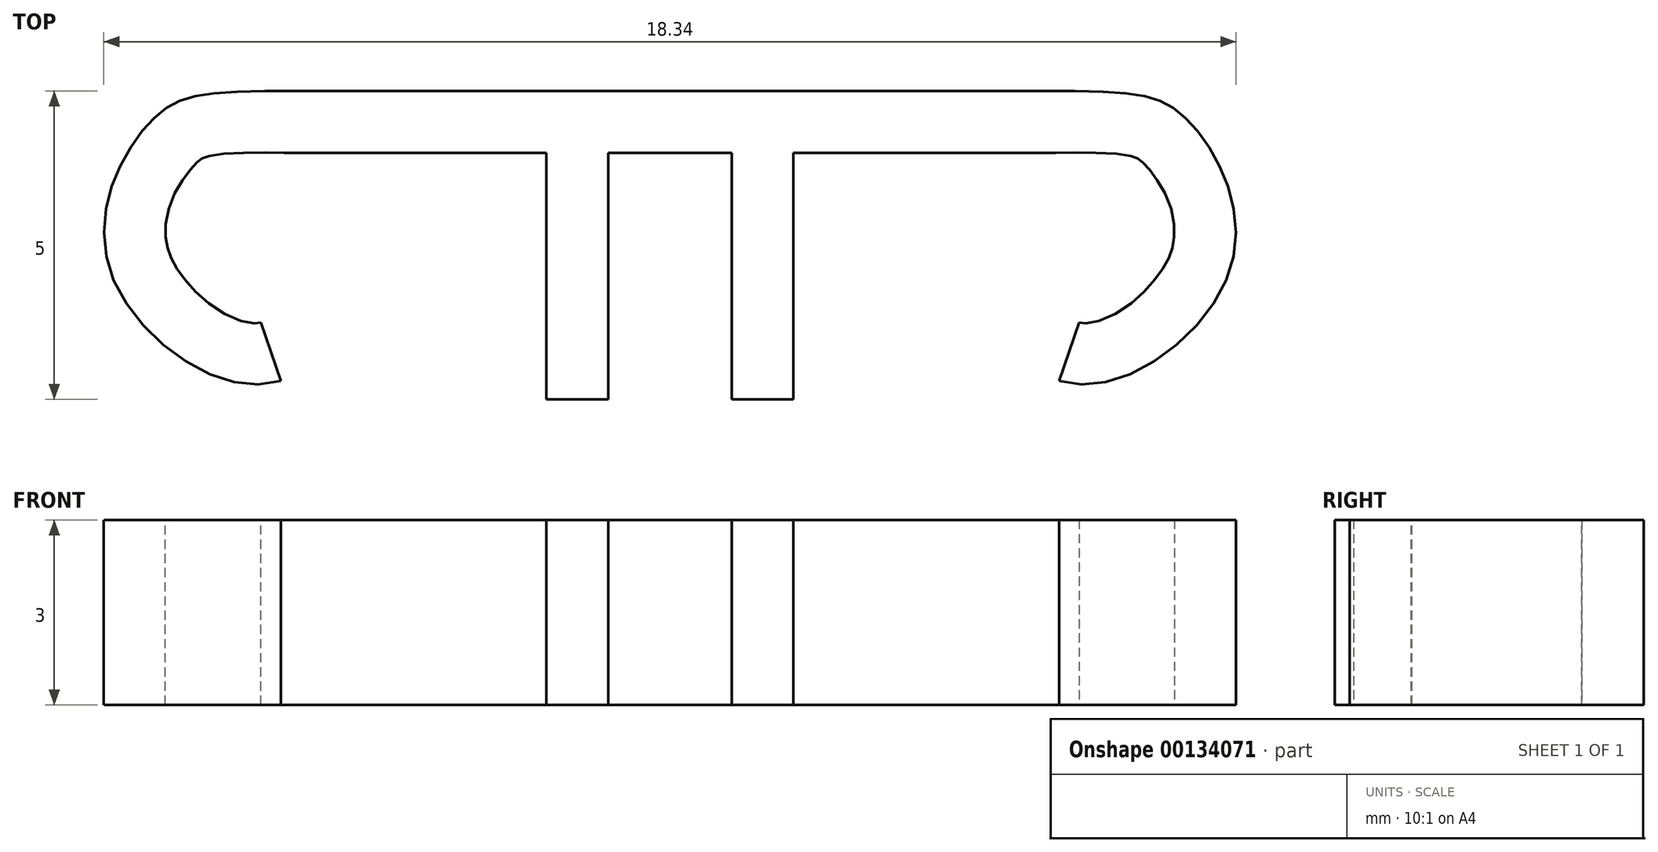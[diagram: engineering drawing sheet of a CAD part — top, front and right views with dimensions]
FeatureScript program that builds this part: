
annotation { "Feature Type Name" : "Feature", "Feature Type Description" : "" }
export const myFeature = defineFeature(function(context is Context, id is Id, definition is map)
    precondition{}
    {
        {
            var Q0;
            Q0=qCreatedBy(makeId("Top.planeOp"),FACE);
            var sketch = newSketch(context, id + "F0", { "sketchPlane" : qUnion([Q0])});
            skLineSegment(sketch, "E0", {"start": v(0, 0) * mm, "end": v(2, 0) * mm});
            skLineSegment(sketch, "E1", {"start": v(2, 0) * mm, "end": v(6, 0) * mm});
            skFitSpline(sketch, "E2", {"points": [v(6, 0) * mm, v(8.4, -0.49) * mm, v(9.07, -2.9) * mm, v(6.3, -4.7) * mm], "startDerivative": vector(14.13, 0) * mm, "endDerivative": vector(-7.99, 2.7) * mm});
            skLineSegment(sketch, "E3", {"start": v(2, 0) * mm, "end": v(2, -5) * mm});
            skLineSegment(sketch, "E4", {"start": v(2, -5) * mm, "end": v(1, -5) * mm});
            skLineSegment(sketch, "E5", {"start": v(1, -5) * mm, "end": v(1, 0) * mm});
            skLineSegment(sketch, "E6", {"start": v(6, -1) * mm, "end": v(2, -1) * mm});
            skFitSpline(sketch, "E7.0", {"points": [v(6, -1) * mm, v(6.3, -1) * mm, v(6.8, -1) * mm, v(7.3, -1.02) * mm, v(7.5, -1.06) * mm, v(7.56, -1.09) * mm, v(7.58, -1.1) * mm, v(7.62, -1.12) * mm, v(7.67, -1.17) * mm, v(7.76, -1.26) * mm, v(7.88, -1.42) * mm, v(8.02, -1.66) * mm, v(8.14, -1.98) * mm, v(8.17, -2.23) * mm, v(8.16, -2.42) * mm, v(8.14, -2.55) * mm, v(8.09, -2.69) * mm, v(8, -2.85) * mm, v(7.88, -3.02) * mm, v(7.69, -3.24) * mm, v(7.39, -3.5) * mm, v(7.01, -3.7) * mm, v(6.76, -3.76) * mm, v(6.66, -3.76) * mm, v(6.63, -3.75) * mm, v(6.62, -3.75) * mm]});
            skLineSegment(sketch, "E8", {"start": v(6.3, -4.7) * mm, "end": v(6.63, -3.75) * mm});
            skLineSegment(sketch, "E9", {"start": v(0, 0) * mm, "end": v(0, -1) * mm});
            skLineSegment(sketch, "E10", {"start": v(0, -1) * mm, "end": v(1, -1) * mm});
            skLineSegment(sketch, "E11.MirrorCS", {"start": v(0, -1) * mm, "end": v(-1, -1) * mm});
            skLineSegment(sketch, "E12.MirrorCS", {"start": v(0, 0) * mm, "end": v(-2, 0) * mm});
            skLineSegment(sketch, "E13.MirrorCS", {"start": v(-2, 0) * mm, "end": v(-6, 0) * mm});
            skFitSpline(sketch, "E14.MirrorCS", {"points": [v(-6, 0) * mm, v(-8.4, -0.49) * mm, v(-9.07, -2.9) * mm, v(-6.3, -4.7) * mm], "startDerivative": vector(-14.13, 0) * mm, "endDerivative": vector(7.99, 2.7) * mm});
            skLineSegment(sketch, "E15.MirrorCS", {"start": v(-6.3, -4.7) * mm, "end": v(-6.63, -3.75) * mm});
            skLineSegment(sketch, "E16.MirrorCS", {"start": v(-6, -1) * mm, "end": v(-2, -1) * mm});
            skLineSegment(sketch, "E17.MirrorCS", {"start": v(-2, 0) * mm, "end": v(-2, -5) * mm});
            skLineSegment(sketch, "E18.MirrorCS", {"start": v(-2, -5) * mm, "end": v(-1, -5) * mm});
            skLineSegment(sketch, "E19.MirrorCS", {"start": v(-1, -5) * mm, "end": v(-1, 0) * mm});
            skFitSpline(sketch, "E20.0", {"points": [v(-6, -1) * mm, v(-6.3, -1) * mm, v(-6.8, -1) * mm, v(-7.3, -1.02) * mm, v(-7.5, -1.06) * mm, v(-7.56, -1.09) * mm, v(-7.58, -1.1) * mm, v(-7.62, -1.12) * mm, v(-7.67, -1.17) * mm, v(-7.76, -1.26) * mm, v(-7.88, -1.42) * mm, v(-8.02, -1.66) * mm, v(-8.14, -1.98) * mm, v(-8.17, -2.23) * mm, v(-8.16, -2.42) * mm, v(-8.14, -2.55) * mm, v(-8.09, -2.69) * mm, v(-8, -2.85) * mm, v(-7.88, -3.02) * mm, v(-7.69, -3.24) * mm, v(-7.39, -3.5) * mm, v(-7.01, -3.7) * mm, v(-6.76, -3.76) * mm, v(-6.66, -3.76) * mm, v(-6.63, -3.75) * mm, v(-6.62, -3.75) * mm]});
            skSolve(sketch);
        }
        {
            var Q0;
            Q0 = qSketchRegion(id + "F0", true);
            extrude(context, id + "F1", {"entities" : qUnion([Q0]), "depth" : 3 * mm});
        }
    });
